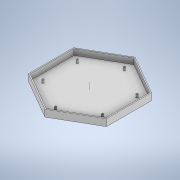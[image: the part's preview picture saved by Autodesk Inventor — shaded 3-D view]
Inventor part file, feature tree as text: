
AUTODESK INVENTOR PART (.ipt)
format: ipt  version: 2020 (Build 240168000, 168)  size: 141,824 bytes
history: native  units: in
note: dims shown in document units (in); Inventor stores cm internally (conversion verified against a paired STEP export)
features: other x5, sketch x4, extrude x3, hole x1, pattern_circular x1
ambient origin geometry x8: Origin, YZ Plane, XZ Plane, XY Plane, X Axis, Y Axis, Z Axis, Center Point
bodies: Solid1 (feature_tree)
feature tree (14):
  extrude  "Extrusion1"  Depth=3.3465in
  extrude  "Extrusion2"  TaperAngle=0.0deg  [1 undecoded]
  extrude  "Extrusion3"  Depth=0.4331in TaperAngle=0.0deg
  hole  "Hole1"  [1 undecoded]
  pattern_circular  "Circular Pattern1"  [2 undecoded]
  sketch  "Sketch1"  dims[d0=0.0in d1=3.3465in]
  sketch  "Sketch2"  dims[d2=0.5118in d3=0.0in d6=0.0in]
  sketch  "Sketch3"  dims[d7=0.0787in d8=0.4331in d9=0.0in]
  sketch  "Sketch4"  dims[d10=0.1575in d11=2.5591in d12=0.1969in d13=0.0in d14=2.5591in d15=0.0in d16=0.0591in d17=0.2362in d18=0.1575in d19=0.0787in d20=90.0deg d21=0.315in d22=0.8108in d23=2.3622in d24=360.0deg]
  other  "Work Axis1"
  other  "Work Axis2"
  other  "Work Axis3"
  other  "Work Axis4"
  other  "Work Axis5"
note: 4 required parameter values undecoded (feature->parameter linkage not recoverable at this tier; creation-order binding heuristic only, values carry confidence <= 0.55)
